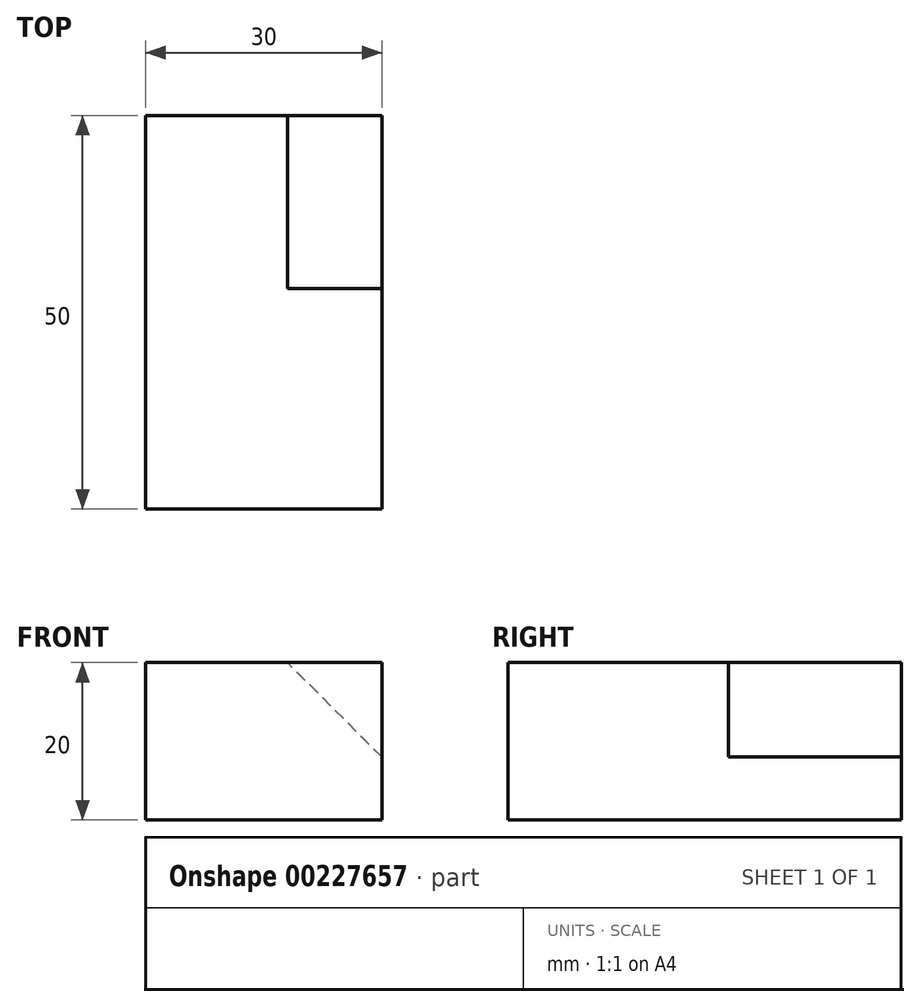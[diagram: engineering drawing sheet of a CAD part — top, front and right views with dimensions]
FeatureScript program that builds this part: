
annotation { "Feature Type Name" : "Feature", "Feature Type Description" : "" }
export const myFeature = defineFeature(function(context is Context, id is Id, definition is map)
    precondition{}
    {
        {
            var Q0;
            Q0=qCreatedBy(makeId("Front.planeOp"),FACE);
            var sketch = newSketch(context, id + "F0", { "sketchPlane" : qUnion([Q0])});
            skLineSegment(sketch, "E0.bottom", {"start": v(15, -10) * mm, "end": v(-15, -10) * mm});
            skLineSegment(sketch, "E0.top", {"start": v(15, 10) * mm, "end": v(-15, 10) * mm});
            skLineSegment(sketch, "E0.left", {"start": v(15, -10) * mm, "end": v(15, 10) * mm});
            skLineSegment(sketch, "E0.right", {"start": v(-15, -10) * mm, "end": v(-15, 10) * mm});
            skPoint(sketch, "E0.middle", {"position": v(0, 0) * mm});
            skPoint(sketch, "E1", {"position": v(15, -2) * mm});
            skPoint(sketch, "E2", {"position": v(3, 10) * mm});
            skLineSegment(sketch, "E3", {"start": v(15, -2) * mm, "end": v(3, 10) * mm});
            skSolve(sketch);
        }
        {
            var Q0;
            {var subQ2=sQuery(id+"F0.wireOp",EDGE,"E0.bottom");Q0=makeQuery(id+"F0.imprint","IMPRINT",FACE,{"disambiguationData":[TD([[makeQuery(id+"F0.imprint","IMPRINT",EDGE,{"derivedFrom":subQ2}),-1.0]])]});}
            var Q1;
            {var subQ3=sQuery(id+"F0.wireOp",EDGE,"E3");Q1=makeQuery(id+"F0.imprint","IMPRINT",FACE,{"disambiguationData":[TD([[makeQuery(id+"F0.imprint","IMPRINT",EDGE,{"derivedFrom":subQ3}),-1.0]])]});}
            extrude(context, id + "F1", {"entities" : qUnion([Q0, Q1]), "depth" : 50 * mm});
        }
        {
            var Q0;
            {var subQ3=sQuery(id+"F0.wireOp",EDGE,"E3");Q0=makeQuery(id+"F0.imprint","IMPRINT",FACE,{"disambiguationData":[TD([[makeQuery(id+"F0.imprint","IMPRINT",EDGE,{"derivedFrom":subQ3}),-1.0]])]});}
            extrude(context, id + "F2", {"entities" : qUnion([Q0]), "operationType" : NewBodyOperationType.REMOVE, "depth" : 22 * mm});
        }
    });
